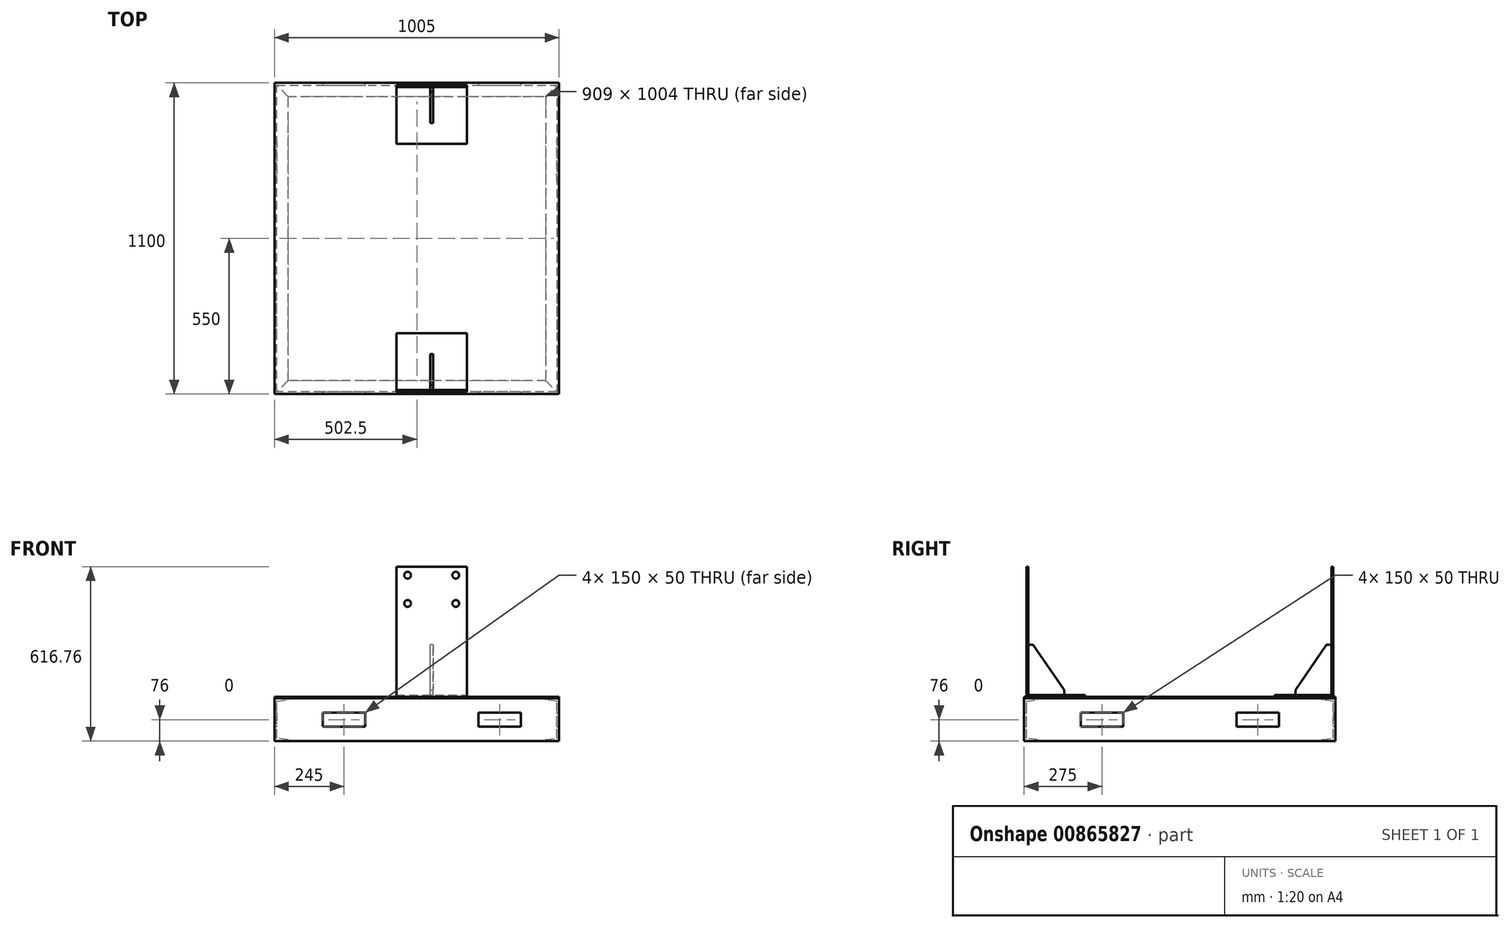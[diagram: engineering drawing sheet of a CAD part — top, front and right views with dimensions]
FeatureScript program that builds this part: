
annotation { "Feature Type Name" : "Feature", "Feature Type Description" : "" }
export const myFeature = defineFeature(function(context is Context, id is Id, definition is map)
    precondition{}
    {
        {
            var Q0;
            Q0=qCreatedBy(makeId("Top.planeOp"),FACE);
            var sketch = newSketch(context, id + "F0", { "sketchPlane" : qUnion([Q0])});
            skLineSegment(sketch, "E0.bottom", {"start": v(502.5, -550) * mm, "end": v(-502.5, -550) * mm});
            skLineSegment(sketch, "E0.top", {"start": v(502.5, 550) * mm, "end": v(-502.5, 550) * mm});
            skLineSegment(sketch, "E0.left", {"start": v(502.5, -550) * mm, "end": v(502.5, 550) * mm});
            skLineSegment(sketch, "E0.right", {"start": v(-502.5, -550) * mm, "end": v(-502.5, 550) * mm});
            skPoint(sketch, "E0.middle", {"position": v(0, 0) * mm});
            skSolve(sketch);
        }
        {
            var Q0;
            Q0 = qSketchRegion(id + "F0", true);
            extrude(context, id + "F1", {"entities" : qUnion([Q0]), "depth" : 4.76 * mm, "offsetDistance" : 25 * mm});
        }
        {
            var Q0;
            Q0=qCreatedBy(makeId("Front.planeOp"),FACE);
            var sketch = newSketch(context, id + "F2", { "sketchPlane" : qUnion([Q0])});
            skPoint(sketch, "E1.0", {"position": v(502.5, 0) * mm});
            skLineSegment(sketch, "E2", {"start": v(502.5, 0) * mm, "end": v(502.5, -152) * mm});
            skLineSegment(sketch, "E3", {"start": v(502.5, -152) * mm, "end": v(454.5, -152) * mm});
            skLineSegment(sketch, "E4", {"start": v(454.5, -152) * mm, "end": v(454.5, -148.72) * mm});
            skLineSegment(sketch, "E5", {"start": v(456.2, -146.74) * mm, "end": v(492.8, -141.26) * mm});
            skLineSegment(sketch, "E6", {"start": v(494.5, -139.28) * mm, "end": v(494.5, -12.72) * mm});
            skLineSegment(sketch, "E7", {"start": v(492.8, -10.74) * mm, "end": v(456.2, -5.26) * mm});
            skLineSegment(sketch, "E8", {"start": v(454.5, -3.28) * mm, "end": v(454.5, 0) * mm});
            skLineSegment(sketch, "E9", {"start": v(454.5, 0) * mm, "end": v(502.5, 0) * mm});
            skPoint(sketch, "E10.visualSharp", {"position": v(454.5, -5) * mm});
            skArc(sketch, "E10.filletArc", {"start": v(454.5, -3.28) * mm, "mid": v(454.98, -4.58) * mm, "end": v(456.2, -5.26) * mm});
            skPoint(sketch, "E11.visualSharp", {"position": v(494.5, -11) * mm});
            skArc(sketch, "E11.filletArc", {"start": v(494.5, -12.72) * mm, "mid": v(494.02, -11.42) * mm, "end": v(492.8, -10.74) * mm});
            skPoint(sketch, "E12.visualSharp", {"position": v(494.5, -141) * mm});
            skArc(sketch, "E12.filletArc", {"start": v(492.8, -141.26) * mm, "mid": v(494.02, -140.58) * mm, "end": v(494.5, -139.28) * mm});
            skPoint(sketch, "E13.visualSharp", {"position": v(454.5, -147) * mm});
            skArc(sketch, "E13.filletArc", {"start": v(456.2, -146.74) * mm, "mid": v(454.98, -147.42) * mm, "end": v(454.5, -148.72) * mm});
            skSolve(sketch);
        }
        {
            var Q0;
            Q0 = qSketchRegion(id + "F2", true);
            var Q1;
            Q1=makeQuery(id+"F1.opExtrude","CAP_EDGE",EDGE,{"disambiguationData":[OSD([sQuery(id+"F0.wireOp",EDGE,"E0.left")])],"isStart":true});
            var Q2;
            Q2=makeQuery(id+"F1.opExtrude","CAP_EDGE",EDGE,{"disambiguationData":[OSD([sQuery(id+"F0.wireOp",EDGE,"E0.bottom")])],"isStart":true});
            var Q3;
            Q3=makeQuery(id+"F1.opExtrude","CAP_EDGE",EDGE,{"disambiguationData":[OSD([sQuery(id+"F0.wireOp",EDGE,"E0.right")])],"isStart":true});
            var Q4;
            Q4=makeQuery(id+"F1.opExtrude","CAP_EDGE",EDGE,{"disambiguationData":[OSD([sQuery(id+"F0.wireOp",EDGE,"E0.top")])],"isStart":true});
            sweep(context, id + "F3", {"profiles" : qUnion([Q0]), "path" : qUnion([Q1, Q2, Q3, Q4])});
        }
        {
            var Q0;
            Q0=makeQuery(id+"F3.opSweep","SWEPT_FACE",FACE,{"disambiguationData":[OSD([sQuery(id+"F0.wireOp",EDGE,"E0.left"),sQuery(id+"F2.wireOp",EDGE,"E2")])]});
            var sketch = newSketch(context, id + "F4", { "sketchPlane" : qUnion([Q0])});
            skLineSegment(sketch, "E14.bottom", {"start": v(-350, -51) * mm, "end": v(-200, -51) * mm});
            skLineSegment(sketch, "E14.top", {"start": v(-350, -101) * mm, "end": v(-200, -101) * mm});
            skLineSegment(sketch, "E14.left", {"start": v(-350, -51) * mm, "end": v(-350, -101) * mm});
            skLineSegment(sketch, "E14.right", {"start": v(-200, -51) * mm, "end": v(-200, -101) * mm});
            skLineSegment(sketch, "E15.bottom", {"start": v(350, -51) * mm, "end": v(200, -51) * mm});
            skLineSegment(sketch, "E15.top", {"start": v(350, -101) * mm, "end": v(200, -101) * mm});
            skLineSegment(sketch, "E15.left", {"start": v(350, -51) * mm, "end": v(350, -101) * mm});
            skLineSegment(sketch, "E15.right", {"start": v(200, -51) * mm, "end": v(200, -101) * mm});
            skSolve(sketch);
        }
        {
            var Q0;
            Q0 = qSketchRegion(id + "F4", true);
            extrude(context, id + "F5", {"entities" : qUnion([Q0]), "operationType" : NewBodyOperationType.REMOVE, "endBound" : BoundingType.THROUGH_ALL, "oppositeDirection" : true, "depth" : 25 * mm, "offsetDistance" : 25 * mm});
        }
        {
            var Q0;
            Q0=makeQuery(id+"F3.opSweep","SWEPT_FACE",FACE,{"disambiguationData":[OSD([sQuery(id+"F0.wireOp",EDGE,"E0.bottom"),sQuery(id+"F2.wireOp",EDGE,"E2")])]});
            var sketch = newSketch(context, id + "F6", { "sketchPlane" : qUnion([Q0])});
            skLineSegment(sketch, "E16.bottom", {"start": v(-332.5, -51) * mm, "end": v(-182.5, -51) * mm});
            skLineSegment(sketch, "E16.top", {"start": v(-332.5, -101) * mm, "end": v(-182.5, -101) * mm});
            skLineSegment(sketch, "E16.left", {"start": v(-332.5, -51) * mm, "end": v(-332.5, -101) * mm});
            skLineSegment(sketch, "E16.right", {"start": v(-182.5, -51) * mm, "end": v(-182.5, -101) * mm});
            skLineSegment(sketch, "E17.bottom", {"start": v(217.5, -51) * mm, "end": v(367.5, -51) * mm});
            skLineSegment(sketch, "E17.top", {"start": v(217.5, -101) * mm, "end": v(367.5, -101) * mm});
            skLineSegment(sketch, "E17.left", {"start": v(217.5, -51) * mm, "end": v(217.5, -101) * mm});
            skLineSegment(sketch, "E17.right", {"start": v(367.5, -51) * mm, "end": v(367.5, -101) * mm});
            skSolve(sketch);
        }
        {
            var Q0;
            Q0 = qSketchRegion(id + "F6", true);
            extrude(context, id + "F7", {"entities" : qUnion([Q0]), "operationType" : NewBodyOperationType.REMOVE, "endBound" : BoundingType.THROUGH_ALL, "oppositeDirection" : true, "depth" : 25 * mm, "offsetDistance" : 25 * mm});
        }
        {
            var Q0;
            Q0=makeQuery(id+"F1.opExtrude","CAP_FACE",FACE,{"disambiguationData":[OSD([sQuery(id+"F0.wireOp",EDGE,"E0.bottom"),sQuery(id+"F0.wireOp",EDGE,"E0.top"),sQuery(id+"F0.wireOp",EDGE,"E0.left"),sQuery(id+"F0.wireOp",EDGE,"E0.right")])],"isStart":false});
            var sketch = newSketch(context, id + "F8", { "sketchPlane" : qUnion([Q0])});
            skLineSegment(sketch, "E18.bottom", {"start": v(-72.5, -535) * mm, "end": v(177.5, -535) * mm});
            skLineSegment(sketch, "E18.top", {"start": v(-72.5, -335) * mm, "end": v(177.5, -335) * mm});
            skLineSegment(sketch, "E18.left", {"start": v(-72.5, -535) * mm, "end": v(-72.5, -335) * mm});
            skLineSegment(sketch, "E18.right", {"start": v(177.5, -535) * mm, "end": v(177.5, -335) * mm});
            skSolve(sketch);
        }
        {
            var Q0;
            Q0 = qSketchRegion(id + "F8", true);
            extrude(context, id + "F9", {"entities" : qUnion([Q0]), "depth" : 6.35 * mm, "offsetDistance" : 25 * mm});
        }
        {
            var Q0;
            Q0=makeQuery(id+"F1.opExtrude","CAP_FACE",FACE,{"disambiguationData":[OSD([sQuery(id+"F0.wireOp",EDGE,"E0.bottom"),sQuery(id+"F0.wireOp",EDGE,"E0.top"),sQuery(id+"F0.wireOp",EDGE,"E0.left"),sQuery(id+"F0.wireOp",EDGE,"E0.right")])],"isStart":false});
            var sketch = newSketch(context, id + "F10", { "sketchPlane" : qUnion([Q0])});
            skLineSegment(sketch, "E19.0", {"start": v(-72.5, -535) * mm, "end": v(177.5, -535) * mm});
            skLineSegment(sketch, "E20", {"start": v(-72.5, -535) * mm, "end": v(-72.5, -541.35) * mm});
            skLineSegment(sketch, "E21", {"start": v(-72.5, -541.35) * mm, "end": v(177.5, -541.35) * mm});
            skLineSegment(sketch, "E22", {"start": v(177.5, -541.35) * mm, "end": v(177.5, -535) * mm});
            skSolve(sketch);
        }
        {
            var Q0;
            Q0 = qSketchRegion(id + "F10", true);
            extrude(context, id + "F11", {"entities" : qUnion([Q0]), "depth" : 460 * mm, "offsetDistance" : 25 * mm});
        }
        {
            var Q0;
            Q0=makeQuery(id+"F11.opExtrude","SWEPT_FACE",FACE,{"disambiguationData":[OSD([sQuery(id+"F10.wireOp",EDGE,"E19.0")])]});
            var sketch = newSketch(context, id + "F12", { "sketchPlane" : qUnion([Q0])});
            skPoint(sketch, "E23.0", {"position": v(-52.5, 11.1) * mm});
            skLineSegment(sketch, "E24.bottom", {"start": v(-57.26, 11.1) * mm, "end": v(-47.74, 11.1) * mm});
            skLineSegment(sketch, "E24.top", {"start": v(-57.26, 189.11) * mm, "end": v(-47.74, 189.11) * mm});
            skLineSegment(sketch, "E24.left", {"start": v(-57.26, 11.1) * mm, "end": v(-57.26, 189.11) * mm});
            skLineSegment(sketch, "E24.right", {"start": v(-47.74, 11.11) * mm, "end": v(-47.74, 189.11) * mm});
            skSolve(sketch);
        }
        {
            var Q0;
            Q0 = qSketchRegion(id + "F12", true);
            extrude(context, id + "F13", {"entities" : qUnion([Q0]), "depth" : 127 * mm, "offsetDistance" : 25 * mm});
        }
        {
            var Q0;
            Q0=makeQuery(id+"F13.opExtrude","CAP_EDGE",EDGE,{"disambiguationData":[OSD([sQuery(id+"F12.wireOp",EDGE,"E24.top")])],"isStart":false});
            chamfer(context, id + "F14", {"entities" : qUnion([Q0]), "chamferType" : ChamferType.TWO_OFFSETS, "width1" : 110 * mm, "oppositeDirection" : false, "width2" : 160 * mm, "tangentPropagation" : true});
        }
        {
            var Q0;
            Q0=makeQuery(id+"F11.opExtrude","SWEPT_FACE",FACE,{"disambiguationData":[OSD([sQuery(id+"F10.wireOp",EDGE,"E19.0")])]});
            var sketch = newSketch(context, id + "F15", { "sketchPlane" : qUnion([Q0])});
            skCircle(sketch, "E25", {"center": v(-137.5, 434.76) * mm, "radius": 12 * mm});
            skCircle(sketch, "E26", {"center": v(32.5, 434.76) * mm, "radius": 12 * mm});
            skCircle(sketch, "E27", {"center": v(-137.5, 334.76) * mm, "radius": 12 * mm});
            skCircle(sketch, "E28", {"center": v(32.5, 334.76) * mm, "radius": 12 * mm});
            skSolve(sketch);
        }
        {
            var Q0;
            Q0 = qSketchRegion(id + "F15", true);
            extrude(context, id + "F16", {"entities" : qUnion([Q0]), "operationType" : NewBodyOperationType.REMOVE, "endBound" : BoundingType.THROUGH_ALL, "oppositeDirection" : true, "depth" : 25 * mm, "offsetDistance" : 25 * mm});
        }
        {
            var Q0;
            Q0=makeQuery(id+"F9.opExtrude","SWEPT_BODY",BODY,{"disambiguationData":[OSD([sQuery(id+"F8.wireOp",EDGE,"E18.bottom"),sQuery(id+"F8.wireOp",EDGE,"E18.top"),sQuery(id+"F8.wireOp",EDGE,"E18.left"),sQuery(id+"F8.wireOp",EDGE,"E18.right")])]});
            var Q1;
            Q1=makeQuery(id+"F13.opExtrude","SWEPT_BODY",BODY,{"disambiguationData":[OSD([sQuery(id+"F12.wireOp",EDGE,"E24.bottom"),sQuery(id+"F12.wireOp",EDGE,"E24.top"),sQuery(id+"F12.wireOp",EDGE,"E24.left"),sQuery(id+"F12.wireOp",EDGE,"E24.right")])]});
            var Q2;
            Q2=makeQuery(id+"F11.opExtrude","SWEPT_BODY",BODY,{"disambiguationData":[OSD([sQuery(id+"F10.wireOp",EDGE,"E19.0"),sQuery(id+"F10.wireOp",EDGE,"E20"),sQuery(id+"F10.wireOp",EDGE,"E21"),sQuery(id+"F10.wireOp",EDGE,"E22")])]});
            var Q3;
            Q3=qCreatedBy(makeId("Front.planeOp"),FACE);
            mirror(context, id + "F17", {"entities" : qUnion([Q0, Q1, Q2]), "mirrorPlane" : qUnion([Q3])});
        }
    });
